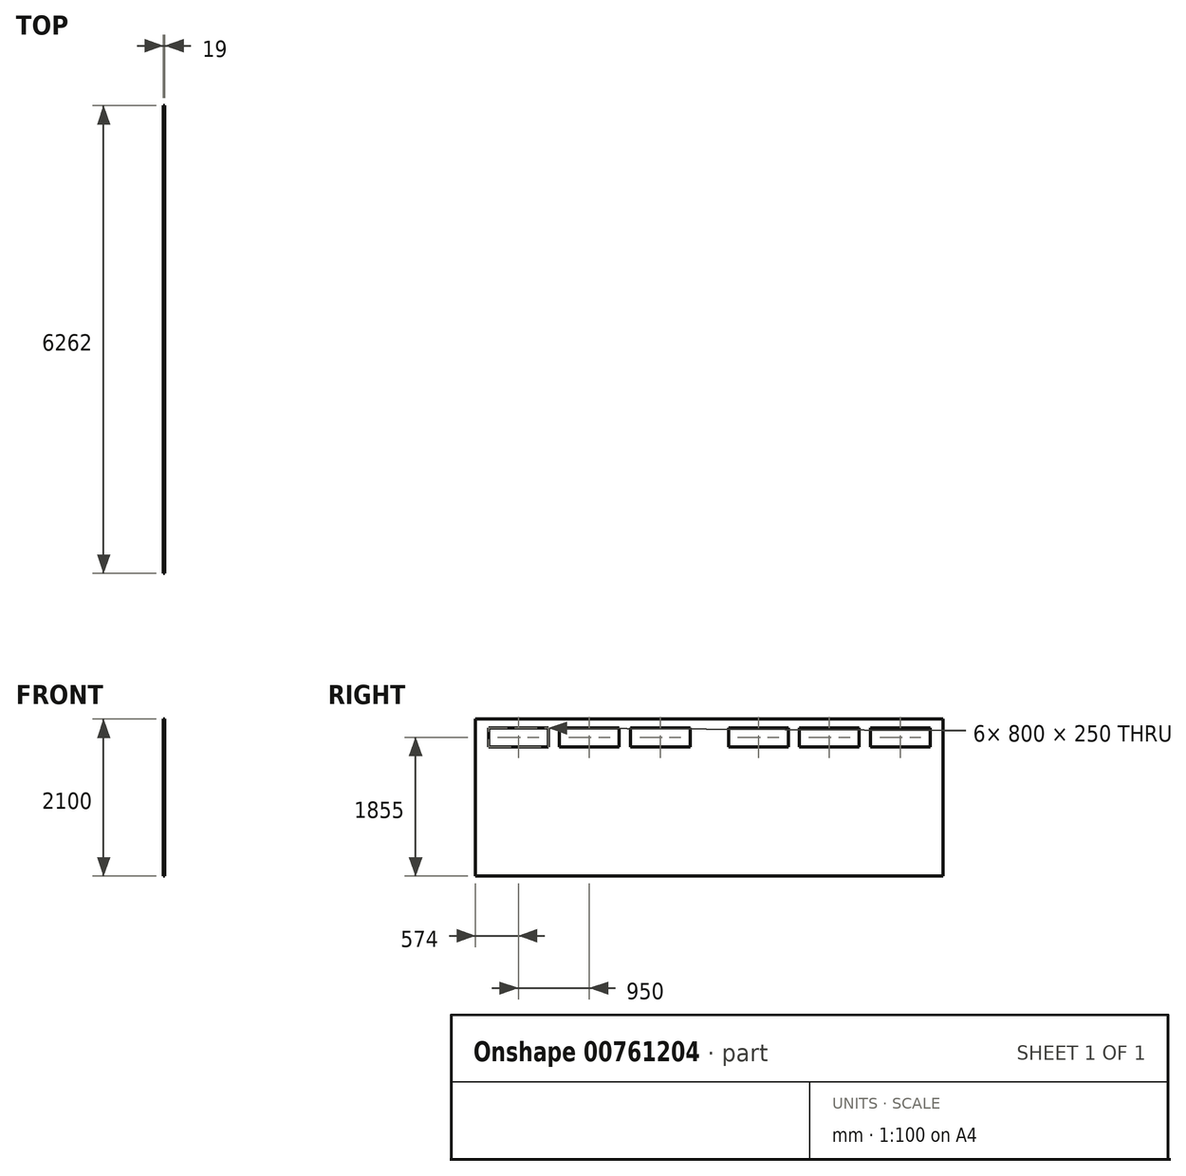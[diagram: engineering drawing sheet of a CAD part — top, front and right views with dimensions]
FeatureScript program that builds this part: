
annotation { "Feature Type Name" : "Feature", "Feature Type Description" : "" }
export const myFeature = defineFeature(function(context is Context, id is Id, definition is map)
    precondition{}
    {
        {
            var Q0;
            Q0=qCreatedBy(makeId("Right.planeOp"),FACE);
            var sketch = newSketch(context, id + "F0", { "sketchPlane" : qUnion([Q0])});
            skLineSegment(sketch, "E0.bottom", {"start": v(0, 0) * mm, "end": v(6262, 0) * mm});
            skLineSegment(sketch, "E0.top", {"start": v(0, 2100) * mm, "end": v(6262, 2100) * mm});
            skLineSegment(sketch, "E0.left", {"start": v(0, 0) * mm, "end": v(0, 2100) * mm});
            skLineSegment(sketch, "E0.right", {"start": v(6262, 0) * mm, "end": v(6262, 2100) * mm});
            skLineSegment(sketch, "E1.bottom", {"start": v(6088, 1980) * mm, "end": v(5288, 1980) * mm});
            skLineSegment(sketch, "E1.top", {"start": v(6088, 1730) * mm, "end": v(5288, 1730) * mm});
            skLineSegment(sketch, "E1.left", {"start": v(6088, 1980) * mm, "end": v(6088, 1730) * mm});
            skLineSegment(sketch, "E1.right", {"start": v(5288, 1980) * mm, "end": v(5288, 1730) * mm});
            skLineSegment(sketch, "E2.bottom", {"start": v(5138, 1980) * mm, "end": v(4338, 1980) * mm});
            skLineSegment(sketch, "E2.top", {"start": v(5138, 1730) * mm, "end": v(4338, 1730) * mm});
            skLineSegment(sketch, "E2.left", {"start": v(5138, 1980) * mm, "end": v(5138, 1730) * mm});
            skLineSegment(sketch, "E2.right", {"start": v(4338, 1980) * mm, "end": v(4338, 1730) * mm});
            skLineSegment(sketch, "E3.bottom", {"start": v(4188, 1980) * mm, "end": v(3388, 1980) * mm});
            skLineSegment(sketch, "E3.top", {"start": v(4188, 1730) * mm, "end": v(3388, 1730) * mm});
            skLineSegment(sketch, "E3.left", {"start": v(4188, 1980) * mm, "end": v(4188, 1730) * mm});
            skLineSegment(sketch, "E3.right", {"start": v(3388, 1980) * mm, "end": v(3388, 1730) * mm});
            skLineSegment(sketch, "E4.bottom", {"start": v(2874, 1980) * mm, "end": v(2074, 1980) * mm});
            skLineSegment(sketch, "E4.top", {"start": v(2874, 1730) * mm, "end": v(2074, 1730) * mm});
            skLineSegment(sketch, "E4.left", {"start": v(2874, 1980) * mm, "end": v(2874, 1730) * mm});
            skLineSegment(sketch, "E4.right", {"start": v(2074, 1980) * mm, "end": v(2074, 1730) * mm});
            skLineSegment(sketch, "E5.bottom", {"start": v(1924, 1980) * mm, "end": v(1124, 1980) * mm});
            skLineSegment(sketch, "E5.top", {"start": v(1924, 1730) * mm, "end": v(1124, 1730) * mm});
            skLineSegment(sketch, "E5.left", {"start": v(1924, 1980) * mm, "end": v(1924, 1730) * mm});
            skLineSegment(sketch, "E5.right", {"start": v(1124, 1980) * mm, "end": v(1124, 1730) * mm});
            skLineSegment(sketch, "E6.bottom", {"start": v(174, 1980) * mm, "end": v(974, 1980) * mm});
            skLineSegment(sketch, "E6.top", {"start": v(174, 1730) * mm, "end": v(974, 1730) * mm});
            skLineSegment(sketch, "E6.left", {"start": v(174, 1980) * mm, "end": v(174, 1730) * mm});
            skLineSegment(sketch, "E6.right", {"start": v(974, 1980) * mm, "end": v(974, 1730) * mm});
            skSolve(sketch);
        }
        {
            var Q0;
            Q0=qSketchRegion(id+"F0",true);
            extrude(context, id + "F1", {"entities" : qUnion([Q0]), "depth" : 19 * mm, "offsetDistance" : 25 * mm});
        }
    });
